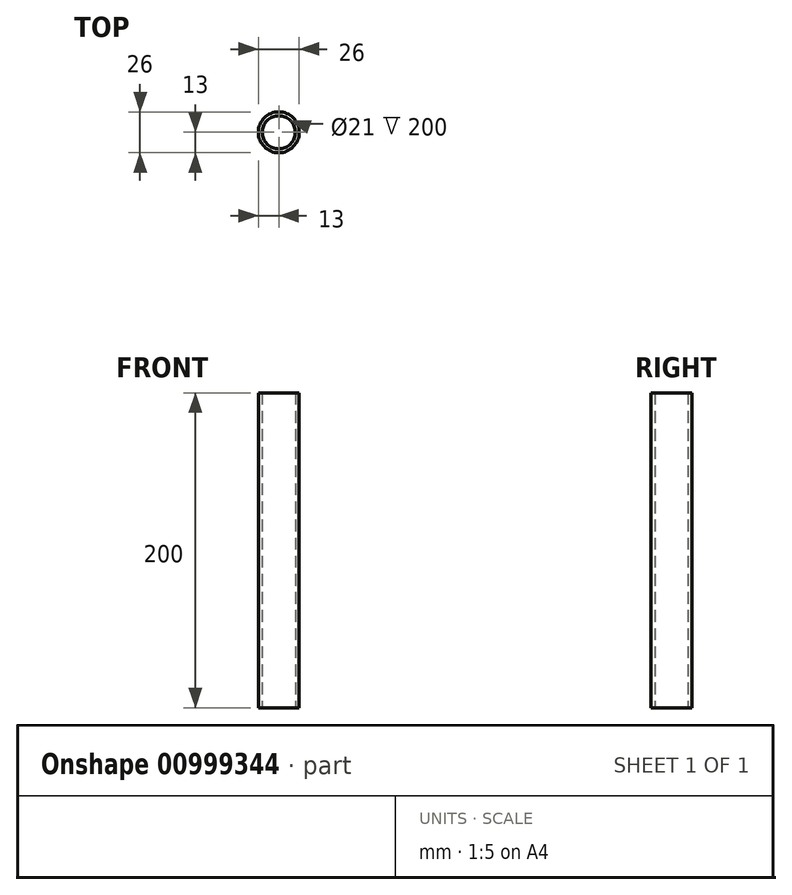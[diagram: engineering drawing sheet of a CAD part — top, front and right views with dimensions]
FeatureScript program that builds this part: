
annotation { "Feature Type Name" : "Feature", "Feature Type Description" : "" }
export const myFeature = defineFeature(function(context is Context, id is Id, definition is map)
    precondition{}
    {
        {
            var Q0;
            Q0=qCreatedBy(makeId("Top.planeOp"),FACE);
            var sketch = newSketch(context, id + "F0", { "sketchPlane" : qUnion([Q0])});
            skCircle(sketch, "E0", {"center": v(0, 0) * mm, "radius": 13 * mm});
            skCircle(sketch, "E1", {"center": v(0, 0) * mm, "radius": 10.5 * mm});
            skSolve(sketch);
        }
        {
            var Q0;
            Q0 = qSketchRegion(id + "F0", true);
            extrude(context, id + "F1", {"entities" : qUnion([Q0]), "endBound" : BoundingType.SYMMETRIC, "depth" : 200 * mm, "offsetDistance" : 25 * mm});
        }
    });
